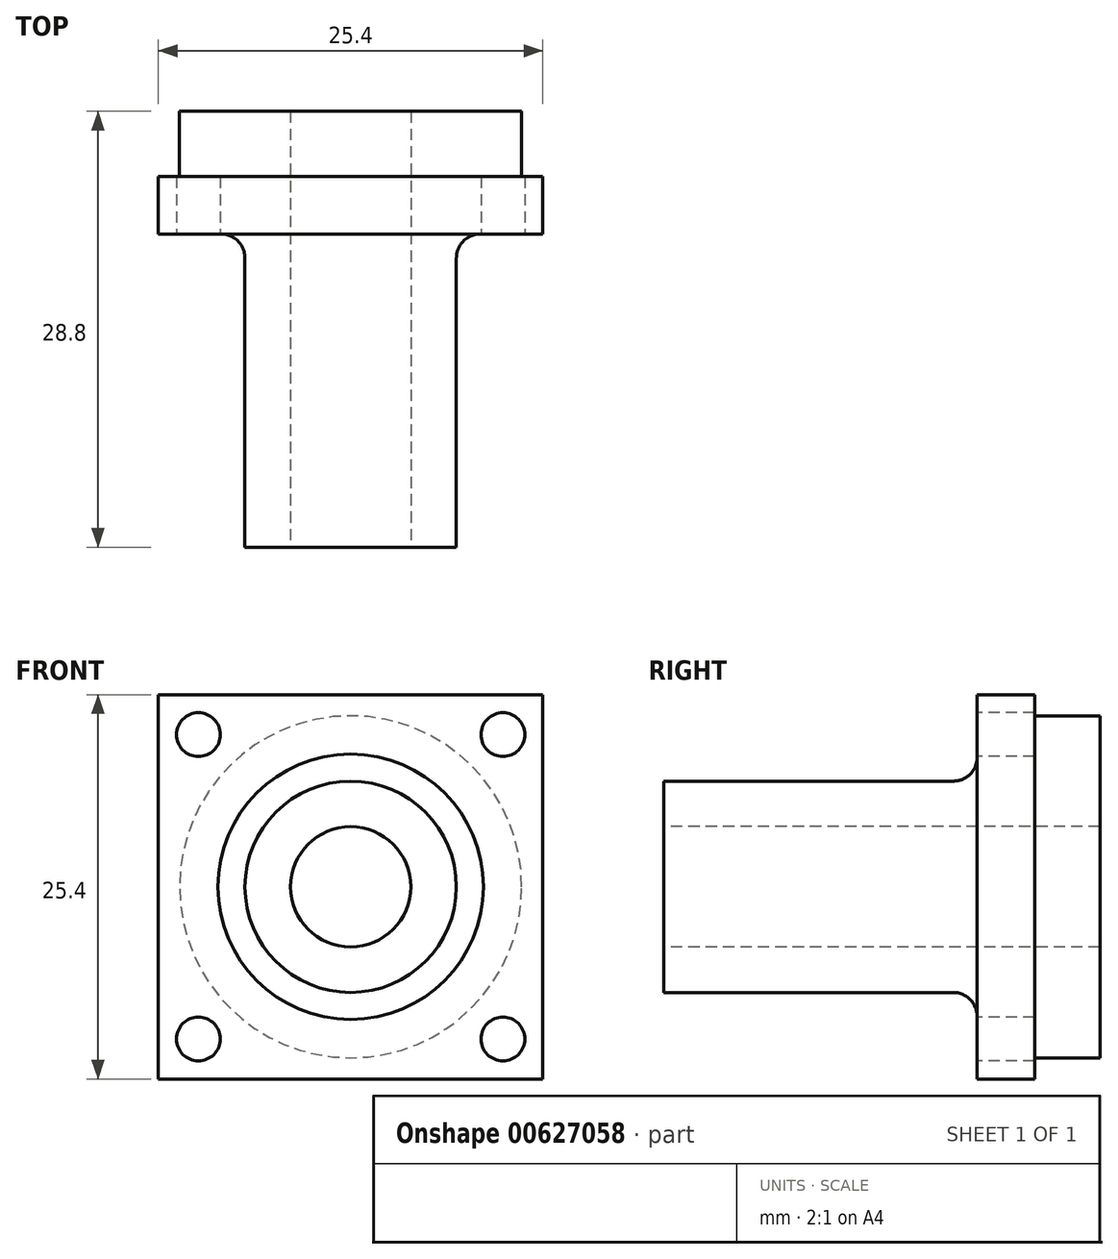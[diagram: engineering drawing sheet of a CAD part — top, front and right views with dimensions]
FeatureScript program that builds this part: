
annotation { "Feature Type Name" : "Feature", "Feature Type Description" : "" }
export const myFeature = defineFeature(function(context is Context, id is Id, definition is map)
    precondition{}
    {
        {
            var Q0;
            Q0=qCreatedBy(makeId("Right.planeOp"),FACE);
            var sketch = newSketch(context, id + "F0", { "sketchPlane" : qUnion([Q0])});
            skLineSegment(sketch, "E0", {"start": v(-11.22, 0) * mm, "end": v(14.67, 0) * mm, "construction": true});
            skLineSegment(sketch, "E1", {"start": v(0, 6.99) * mm, "end": v(19.11, 6.99) * mm});
            skArc(sketch, "E2", {"start": v(19.11, 6.99) * mm, "mid": v(20.3, 7.52) * mm, "end": v(20.68, 8.77) * mm});
            skLineSegment(sketch, "E3", {"start": v(20.68, 8.77) * mm, "end": v(20.68, 12.7) * mm});
            skLineSegment(sketch, "E4", {"start": v(20.68, 12.7) * mm, "end": v(24.49, 12.7) * mm});
            skLineSegment(sketch, "E5", {"start": v(24.49, 12.7) * mm, "end": v(24.49, 11.3) * mm});
            skLineSegment(sketch, "E6", {"start": v(24.49, 11.3) * mm, "end": v(28.8, 11.3) * mm});
            skLineSegment(sketch, "E7", {"start": v(28.8, 11.3) * mm, "end": v(28.8, 3.98) * mm});
            skLineSegment(sketch, "E8", {"start": v(28.8, 3.98) * mm, "end": v(0, 3.98) * mm});
            skLineSegment(sketch, "E9", {"start": v(0, 3.98) * mm, "end": v(0, 6.99) * mm});
            skSolve(sketch);
        }
        {
            var Q0;
            Q0=makeQuery(id+"F0.imprint","IMPRINT",FACE,{"disambiguationData":[TD([[makeQuery(id+"F0.imprint","IMPRINT",EDGE,{"derivedFrom":sQuery(id+"F0.wireOp",EDGE,"E1")}),-1.0]])]});
            var Q1;
            Q1=sQuery(id+"F0.wireOp",EDGE,"E0");
            revolve(context, id + "F1", {"entities" : qUnion([Q0]), "axis" : qUnion([Q1]), "revolveType" : RevolveType.FULL});
        }
        {
            var Q0;
            Q0=makeQuery(id+"F1.opRevolve","SWEPT_FACE",FACE,{"disambiguationData":[OSD([sQuery(id+"F0.wireOp",EDGE,"E3")])]});
            var sketch = newSketch(context, id + "F2", { "sketchPlane" : qUnion([Q0])});
            skLineSegment(sketch, "E10.bottom", {"start": v(12.7, -12.7) * mm, "end": v(-12.7, -12.7) * mm});
            skLineSegment(sketch, "E10.top", {"start": v(12.7, 12.7) * mm, "end": v(-12.7, 12.7) * mm});
            skLineSegment(sketch, "E10.left", {"start": v(12.7, -12.7) * mm, "end": v(12.7, 12.7) * mm});
            skLineSegment(sketch, "E10.right", {"start": v(-12.7, -12.7) * mm, "end": v(-12.7, 12.7) * mm});
            skPoint(sketch, "E10.middle", {"position": v(0, 0) * mm});
            skSolve(sketch);
        }
        {
            var Q0;
            {var subQ0=sQuery(id+"F2.wireOp",EDGE,"E10.right");var subQ1=sQuery(id+"F2.wireOp",EDGE,"E10.top");var subQ2=makeQuery(id+"F2.imprint","INTERSECT",VERTEX,{"derivedFrom":[subQ1,subQ0]});Q0=makeQuery(id+"F2.imprint","IMPRINT",FACE,{"disambiguationData":[TD([[makeQuery(id+"F2.imprint","IMPRINT",EDGE,{"disambiguationData":[TD([[subQ2,1.0]])],"derivedFrom":subQ1}),1.0]])]});}
            var Q1;
            {var subQ0=sQuery(id+"F2.wireOp",EDGE,"E10.left");var subQ1=sQuery(id+"F2.wireOp",EDGE,"E10.top");var subQ2=makeQuery(id+"F2.imprint","INTERSECT",VERTEX,{"derivedFrom":[subQ1,subQ0]});Q1=makeQuery(id+"F2.imprint","IMPRINT",FACE,{"disambiguationData":[TD([[makeQuery(id+"F2.imprint","IMPRINT",EDGE,{"disambiguationData":[TD([[subQ2,-1.0]])],"derivedFrom":subQ1}),1.0]])]});}
            var Q2;
            {var subQ0=sQuery(id+"F2.wireOp",EDGE,"E10.left");var subQ1=sQuery(id+"F2.wireOp",EDGE,"E10.bottom");var subQ2=makeQuery(id+"F2.imprint","INTERSECT",VERTEX,{"derivedFrom":[subQ1,subQ0]});Q2=makeQuery(id+"F2.imprint","IMPRINT",FACE,{"disambiguationData":[TD([[makeQuery(id+"F2.imprint","IMPRINT",EDGE,{"disambiguationData":[TD([[subQ2,-1.0]])],"derivedFrom":subQ1}),-1.0]])]});}
            var Q3;
            {var subQ0=sQuery(id+"F2.wireOp",EDGE,"E10.right");var subQ1=sQuery(id+"F2.wireOp",EDGE,"E10.bottom");var subQ2=makeQuery(id+"F2.imprint","INTERSECT",VERTEX,{"derivedFrom":[subQ1,subQ0]});Q3=makeQuery(id+"F2.imprint","IMPRINT",FACE,{"disambiguationData":[TD([[makeQuery(id+"F2.imprint","IMPRINT",EDGE,{"disambiguationData":[TD([[subQ2,1.0]])],"derivedFrom":subQ1}),-1.0]])]});}
            var Q4;
            Q4=makeQuery(id+"F1.opRevolve","SWEPT_FACE",FACE,{"disambiguationData":[OSD([sQuery(id+"F0.wireOp",EDGE,"E5")])]});
            extrude(context, id + "F3", {"entities" : qUnion([Q0, Q1, Q2, Q3]), "operationType" : NewBodyOperationType.ADD, "endBound" : BoundingType.UP_TO_SURFACE, "oppositeDirection" : true, "depth" : 25.4 * mm, "endBoundEntityFace" : qUnion([Q4]), "offsetDistance" : 25.4 * mm});
        }
        {
            var Q0;
            {var subQ0=sQuery(id+"F2.wireOp",EDGE,"E10.right");var subQ1=sQuery(id+"F2.wireOp",EDGE,"E10.top");var subQ2=sQuery(id+"F0.wireOp",EDGE,"E4");var subQ3=sQuery(id+"F0.wireOp",EDGE,"E3");var subQ4=sQuery(id+"F2.wireOp",EDGE,"E10.left");var subQ5=sQuery(id+"F2.wireOp",EDGE,"E10.bottom");Q0=makeQuery(id+"F3.boolean.opBoolean","MERGE",FACE,{"derivedFrom":[makeQuery(id+"F1.opRevolve","SWEPT_FACE",FACE,{"disambiguationData":[OSD([subQ3])]}),makeQuery(id+"F3.opExtrude","CAP_FACE",FACE,{"disambiguationData":[OSD([subQ3,subQ2,subQ5,subQ4])],"isStart":true}),makeQuery(id+"F3.opExtrude","CAP_FACE",FACE,{"disambiguationData":[OSD([subQ3,subQ2,subQ5,subQ0])],"isStart":true}),makeQuery(id+"F3.opExtrude","CAP_FACE",FACE,{"disambiguationData":[OSD([subQ3,subQ2,subQ1,subQ4])],"isStart":true}),makeQuery(id+"F3.opExtrude","CAP_FACE",FACE,{"disambiguationData":[OSD([subQ3,subQ2,subQ1,subQ0])],"isStart":true})]});}
            var sketch = newSketch(context, id + "F4", { "sketchPlane" : qUnion([Q0])});
            skLineSegment(sketch, "E11", {"start": v(0, 0) * mm, "end": v(10.06, 0) * mm, "construction": true});
            skPoint(sketch, "E11.endSnap0", {"position": v(12.7, 0) * mm});
            skLineSegment(sketch, "E12", {"start": v(0, 0) * mm, "end": v(0, -10.06) * mm});
            skCircle(sketch, "E13", {"center": v(10.06, -10.06) * mm, "radius": 1.45 * mm});
            skCircle(sketch, "E14.MirrorC", {"center": v(10.06, 10.06) * mm, "radius": 1.45 * mm});
            skCircle(sketch, "E15.MirrorC", {"center": v(-10.06, -10.06) * mm, "radius": 1.45 * mm});
            skCircle(sketch, "E16.MirrorC", {"center": v(-10.06, 10.06) * mm, "radius": 1.45 * mm});
            skSolve(sketch);
        }
        {
            var Q0;
            Q0 = qSketchRegion(id + "F4", true);
            extrude(context, id + "F5", {"entities" : qUnion([Q0]), "operationType" : NewBodyOperationType.REMOVE, "oppositeDirection" : true, "depth" : 25.4 * mm, "offsetDistance" : 25.4 * mm});
        }
    });
